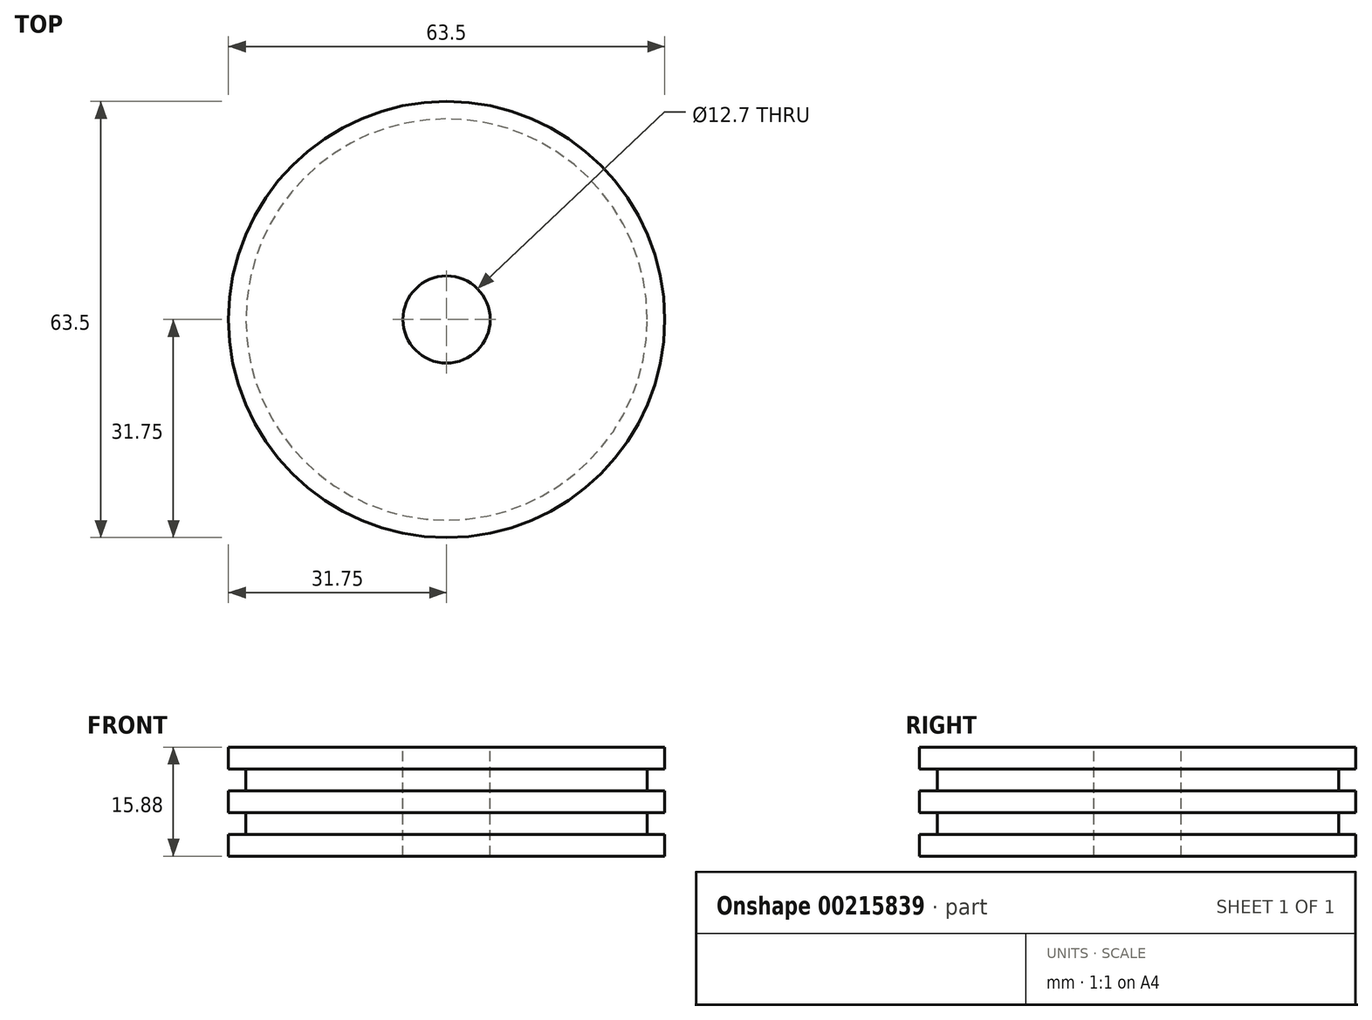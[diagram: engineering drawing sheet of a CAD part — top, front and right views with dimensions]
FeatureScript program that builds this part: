
annotation { "Feature Type Name" : "Feature", "Feature Type Description" : "" }
export const myFeature = defineFeature(function(context is Context, id is Id, definition is map)
    precondition{}
    {
        {
            var Q0;
            Q0=qCreatedBy(makeId("Front.planeOp"),FACE);
            var sketch = newSketch(context, id + "F0", { "sketchPlane" : qUnion([Q0])});
            skLineSegment(sketch, "E0", {"start": v(-6.35, 7.94) * mm, "end": v(-31.75, 7.94) * mm});
            skLineSegment(sketch, "E1", {"start": v(-31.75, 7.94) * mm, "end": v(-31.75, 4.76) * mm});
            skLineSegment(sketch, "E2", {"start": v(-31.75, -1.59) * mm, "end": v(-29.21, -1.59) * mm});
            skLineSegment(sketch, "E3", {"start": v(-29.21, -1.59) * mm, "end": v(-29.21, -4.76) * mm});
            skLineSegment(sketch, "E4", {"start": v(-29.21, -4.76) * mm, "end": v(-31.75, -4.76) * mm});
            skLineSegment(sketch, "E5", {"start": v(-31.75, -4.76) * mm, "end": v(-31.75, -7.94) * mm});
            skLineSegment(sketch, "E6", {"start": v(-31.75, -7.94) * mm, "end": v(-6.35, -7.94) * mm});
            skLineSegment(sketch, "E7", {"start": v(-31.75, 1.59) * mm, "end": v(-29.21, 1.59) * mm});
            skLineSegment(sketch, "E8", {"start": v(-29.21, 1.59) * mm, "end": v(-29.21, 4.76) * mm});
            skLineSegment(sketch, "E9", {"start": v(-29.21, 4.76) * mm, "end": v(-31.75, 4.76) * mm});
            skLineSegment(sketch, "E10.trimOffspring", {"start": v(-31.75, 1.59) * mm, "end": v(-31.75, -1.59) * mm});
            skPoint(sketch, "E11", {"position": v(-31.75, 0) * mm});
            skPoint(sketch, "E12", {"position": v(0, 0) * mm});
            skLineSegment(sketch, "E13", {"start": v(-6.35, 7.94) * mm, "end": v(-6.35, -7.94) * mm});
            skPoint(sketch, "E14", {"position": v(-6.35, 0) * mm});
            skPoint(sketch, "E15.orphan", {"position": v(0, 7.94) * mm});
            skPoint(sketch, "E16.start.orphan", {"position": v(0, -7.94) * mm});
            skLineSegment(sketch, "E17", {"start": v(0, 7.94) * mm, "end": v(0, -7.94) * mm, "construction": true});
            skSolve(sketch);
        }
        {
            var Q0;
            Q0=qSketchRegion(id+"F0",true);
            var Q1;
            Q1=sQuery(id+"F0.wireOp",EDGE,"E17");
            revolve(context, id + "F1", {"entities" : qUnion([Q0]), "axis" : qUnion([Q1]), "revolveType" : RevolveType.FULL});
        }
    });
